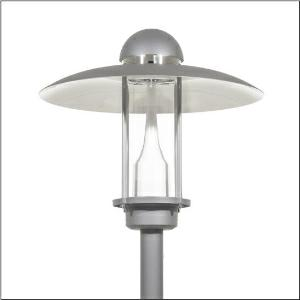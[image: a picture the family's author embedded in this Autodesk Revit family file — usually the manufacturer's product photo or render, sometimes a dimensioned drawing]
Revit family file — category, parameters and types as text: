
# Revit family: city-light_elegance_iq___p1_0a_5xa5265ff14h_a346
name_source: partatom
category: Lighting Fixtures
units: mm (PartAtom-declared; Revit-internal decimal feet)

## family parameters
Cut with Voids When Loaded = No
Host = Face
Light Source = No
Part Type = Normal
Room Calculation Point = No
Round Connector Dimension = Use Diameter
Shared = No

## types (1)
- --- (1 x LED, 1440 lm, 10.5 W, 3000K)
    Apparent Load = 11 VA
    CIE Flux Codes = 32 62 91 97 100
    Color Rendering = 70
    Color Temperature = 3000K
    Default Elevation = 1800 mm
    Description = City-Light Elegance iQ, mast luminaire, Module 540 iQ-SR, primary light control with 3 zone facetted reflector, of plastic, silver coated, highly specular, structured, primary optical cover: cover, of PMMA, transparent, light distribution: P1.0a, light emission: direct distribution, primary light characteristic: strongly asymmetric, installation type: post-top, LED, High Power LED, rated luminous flux: 1.440lm, luminous efficacy: 137lm/W, light colour: 730, colour temperature: 3000K, control gear: ECG iQ, control: Auto-Match, Temp-Guard, Lumen-Switch, Night-Set, Smart-Wire, Light-Fading, Desk-Remote (wireless, voltage-free reading and setting of iQ features in the workshop via application-optimized NFC function/RFID function), optimised constant luminous flux control (CLO 2.0), Street-Remote, presetting dimming logarithmic, with terminal, 6-pole, max. 2.5mm², mains connection: 230..240V, AC, 50/60Hz, start of lifetime: 11W, end of service life: 11W, reduction: 5W, luminaire housing, upper part, of aluminium, coated, Siteco® metallic grey (DB 702S), diameter: 750mm, height: 675mm, spigot size: d x l = 76 x 70mm (post-top) | with reducer (optional accessory) 60 x 70mm, post-top mast mounting element, of diecast aluminium, coated, Siteco® metallic grey (DB 702S), Module 540 iQ-SR, traffic white (RAL 9016), equipment: standard, protection rating (complete): IP65, insulation class (complete): insulation class II (safety insulation), certification: CE, ENEC, VDE, packaging unit: 1 piece

Light Distribution: P1.0a
    Height = 675 mm
    Lamp = 1 x LED
    Lamp Light Flux = 1440 lm
    Lamp Power = 10.5 W
    Lamp count = 1
    Length = 750 mm
    Luminous efficacy = 137 lm/W
    Manufacturer = Siteco
    ModVariant = No
    Model = 5XA5265FF14H
    Number of Poles = 1
    OnlyDefault = Yes
    Power Factor = 1
    Product Name = City-Light Elegance iQ | P1.0a
    Product group = mast luminaire | pylon top
    ProductGroupID = 6100
    Protection Class = Protection class II
    Protection Degree = IP 65
    RLX_Detail_Level = 1
    RLX_Emergency_Light_Flux = 0 lm
    RLX_Emergency_Type = 0
    RLX_Emergency_Type_DB = No
    RlxData = <blob elided: 102057 chars, md5=7db8a653>
    Socket = socket
    Standby Power = 0 W
    System Light Flux = 1440 lm
    System Power = 11 W
    Type Comments = factory setting: luminous flux: 100 % | dim-lin: 254 | 419 mA
    Type Image = l_1006912.jpg
    URL = http://relux.com
    VarID = @adj_092049
    Voltage = 0 V
    Weight = 0.00 kg
    Width = 0 mm  [stored 0 ft]

note: [stored X ft] marks values corroborated as IEEE doubles in the binary element streams (Revit-internal decimal feet)

## geometry (parser evidence)
native form markers: Blend x4, Sweep x9
no freeform markers — native parametric forms only
